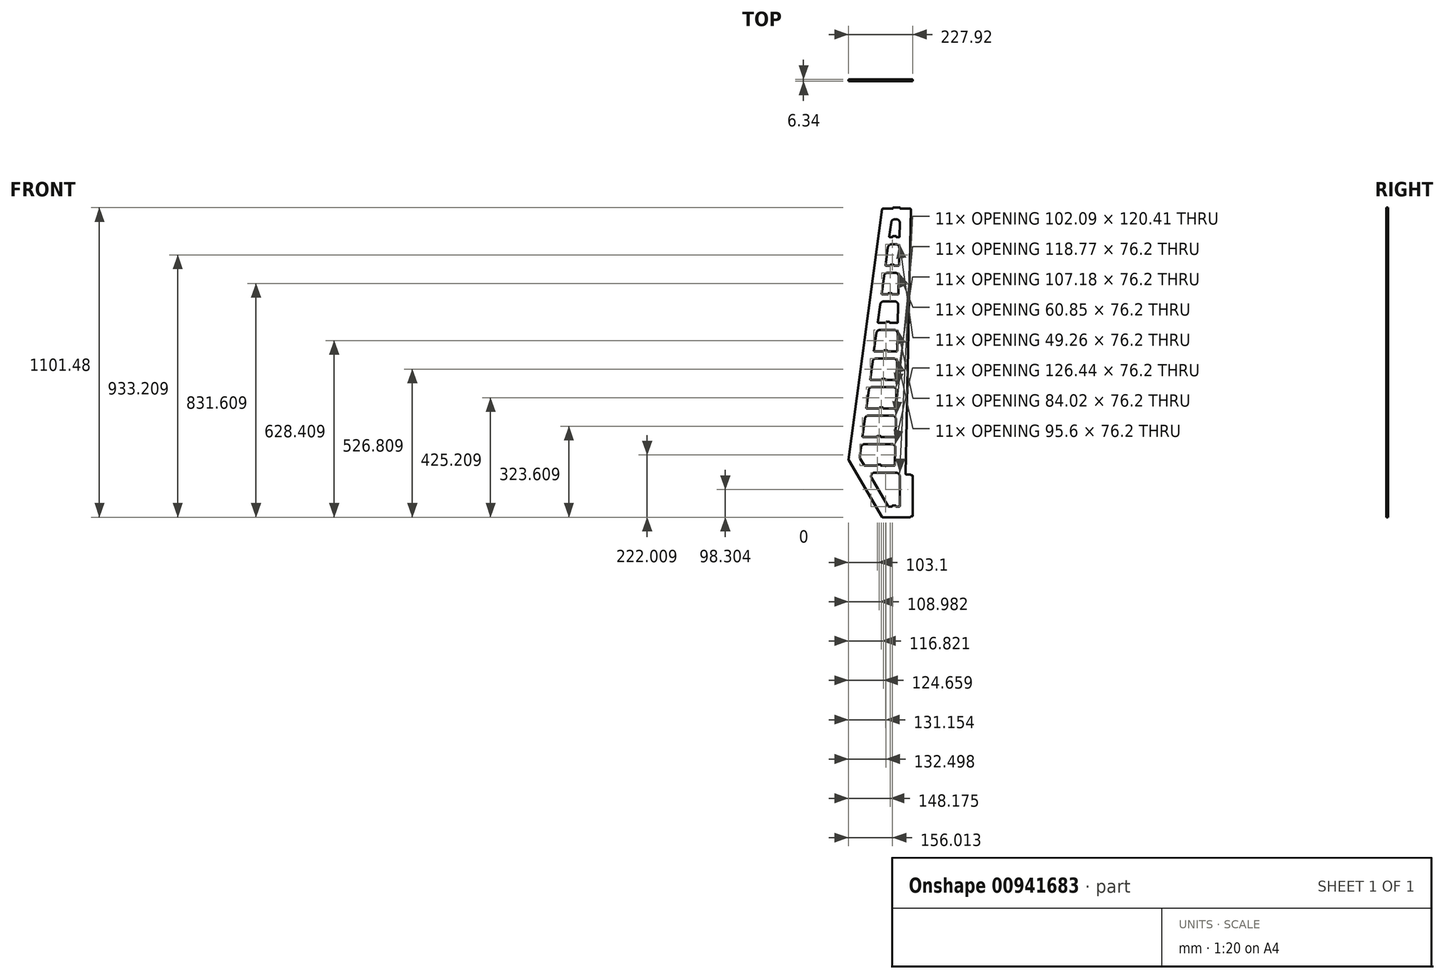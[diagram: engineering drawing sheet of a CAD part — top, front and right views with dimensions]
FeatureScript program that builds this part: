
annotation { "Feature Type Name" : "Feature", "Feature Type Description" : "" }
export const myFeature = defineFeature(function(context is Context, id is Id, definition is map)
    precondition{}
    {
        {
            var Q0;
            Q0=qCreatedBy(makeId("Front.planeOp"),FACE);
            var sketch = newSketch(context, id + "F0", { "sketchPlane" : qUnion([Q0])});
            skLineSegment(sketch, "E0", {"start": v(-3.18, 152.4) * mm, "end": v(-15.81, 152.4) * mm});
            skLineSegment(sketch, "E1", {"start": v(-18.98, 155.64) * mm, "end": v(-0.07, 1095.07) * mm});
            skLineSegment(sketch, "E2", {"start": v(-3.24, 1098.3) * mm, "end": v(-37.78, 1098.3) * mm});
            skLineSegment(sketch, "E3", {"start": v(-101.97, 1095.56) * mm, "end": v(-221.54, 204.3) * mm});
            skLineSegment(sketch, "E4", {"start": v(-221.13, 202.25) * mm, "end": v(-102.52, 1.56) * mm});
            skLineSegment(sketch, "E5", {"start": v(-99.79, 0) * mm, "end": v(-3.17, 0) * mm});
            skLineSegment(sketch, "E6.1", {"start": v(-39.37, 39.69) * mm, "end": v(-39.37, 145.8) * mm});
            skLineSegment(sketch, "E6.2", {"start": v(-51.83, 1060.2) * mm, "end": v(-57.16, 1060.2) * mm});
            skLineSegment(sketch, "E6.3", {"start": v(-69.75, 1049.2) * mm, "end": v(-76.55, 998.5) * mm});
            skLineSegment(sketch, "E6.4", {"start": v(-179.93, 207.43) * mm, "end": v(-166.5, 184.69) * mm});
            skLineSegment(sketch, "E6.5", {"start": v(-56.5, 185.46) * mm, "end": v(-55.25, 247.15) * mm});
            skLineSegment(sketch, "E6.6", {"start": v(-78.95, 38.1) * mm, "end": v(-66.65, 38.1) * mm});
            skLineSegment(sketch, "E7", {"start": v(-41.7, 996.7) * mm, "end": v(-51.8, 996.7) * mm});
            skLineSegment(sketch, "E8", {"start": v(-43.76, 895.1) * mm, "end": v(-59.65, 895.1) * mm});
            skLineSegment(sketch, "E9", {"start": v(-45.8, 793.5) * mm, "end": v(-67.49, 793.5) * mm});
            skLineSegment(sketch, "E10", {"start": v(-47.85, 691.9) * mm, "end": v(-75.33, 691.9) * mm});
            skLineSegment(sketch, "E11", {"start": v(-49.9, 590.3) * mm, "end": v(-83.17, 590.3) * mm});
            skLineSegment(sketch, "E12", {"start": v(-51.94, 488.7) * mm, "end": v(-91.02, 488.7) * mm});
            skLineSegment(sketch, "E13", {"start": v(-53.99, 387.1) * mm, "end": v(-98.86, 387.1) * mm});
            skLineSegment(sketch, "E14", {"start": v(-56.03, 285.5) * mm, "end": v(-106.7, 285.5) * mm});
            skLineSegment(sketch, "E15", {"start": v(-58.08, 183.9) * mm, "end": v(-107, 183.9) * mm});
            skLineSegment(sketch, "E16.0", {"start": v(-52.07, 158.5) * mm, "end": v(-128.76, 158.5) * mm});
            skLineSegment(sketch, "E17.trimOffspring", {"start": v(-139.7, 139.35) * mm, "end": v(-80.32, 38.88) * mm});
            skLineSegment(sketch, "E18.0", {"start": v(-67.95, 260.1) * mm, "end": v(-164.5, 260.1) * mm});
            skLineSegment(sketch, "E19.trimOffspring", {"start": v(-54.45, 287.06) * mm, "end": v(-53.2, 348.75) * mm});
            skLineSegment(sketch, "E20.0", {"start": v(-65.9, 361.7) * mm, "end": v(-150.87, 361.7) * mm});
            skLineSegment(sketch, "E21.trimOffspring", {"start": v(-163.46, 350.7) * mm, "end": v(-172.2, 285.5) * mm});
            skLineSegment(sketch, "E22.trimOffspring", {"start": v(-52.4, 388.66) * mm, "end": v(-51.16, 450.35) * mm});
            skLineSegment(sketch, "E23.0", {"start": v(-63.85, 463.3) * mm, "end": v(-137.24, 463.3) * mm});
            skLineSegment(sketch, "E24.0", {"start": v(-61.8, 564.9) * mm, "end": v(-123.6, 564.9) * mm});
            skLineSegment(sketch, "E25.0", {"start": v(-59.76, 666.5) * mm, "end": v(-109.98, 666.5) * mm});
            skLineSegment(sketch, "E26.0", {"start": v(-57.72, 768.1) * mm, "end": v(-96.35, 768.1) * mm});
            skLineSegment(sketch, "E27.0", {"start": v(-55.67, 869.7) * mm, "end": v(-82.72, 869.7) * mm});
            skLineSegment(sketch, "E28.0", {"start": v(-53.62, 971.3) * mm, "end": v(-69.09, 971.3) * mm});
            skLineSegment(sketch, "E29.trimOffspring", {"start": v(-149.83, 452.3) * mm, "end": v(-158.33, 388.9) * mm});
            skLineSegment(sketch, "E30.trimOffspring", {"start": v(-50.35, 490.26) * mm, "end": v(-49.11, 551.95) * mm});
            skLineSegment(sketch, "E31.trimOffspring", {"start": v(-48.3, 591.86) * mm, "end": v(-47.06, 653.55) * mm});
            skLineSegment(sketch, "E32.trimOffspring", {"start": v(-136.2, 553.9) * mm, "end": v(-144.7, 490.5) * mm});
            skLineSegment(sketch, "E33.trimOffspring", {"start": v(-46.26, 693.46) * mm, "end": v(-45.02, 755.15) * mm});
            skLineSegment(sketch, "E34.trimOffspring", {"start": v(-122.57, 655.5) * mm, "end": v(-131.07, 592.1) * mm});
            skLineSegment(sketch, "E35.trimOffspring", {"start": v(-44.21, 795.06) * mm, "end": v(-42.97, 856.75) * mm});
            skLineSegment(sketch, "E36.trimOffspring", {"start": v(-108.94, 757.1) * mm, "end": v(-117.44, 693.7) * mm});
            skLineSegment(sketch, "E37.trimOffspring", {"start": v(-42.17, 896.66) * mm, "end": v(-40.93, 958.35) * mm});
            skLineSegment(sketch, "E38.trimOffspring", {"start": v(-95.3, 858.7) * mm, "end": v(-103.8, 795.3) * mm});
            skLineSegment(sketch, "E39.trimOffspring", {"start": v(-40.12, 998.26) * mm, "end": v(-39.14, 1047.25) * mm});
            skLineSegment(sketch, "E40.trimOffspring", {"start": v(-81.67, 960.3) * mm, "end": v(-90.18, 896.9) * mm});
            skPoint(sketch, "E41.visualSharp", {"position": v(-161.98, 361.7) * mm});
            skArc(sketch, "E41.filletArc", {"start": v(-150.87, 361.7) * mm, "mid": v(-159.23, 358.57) * mm, "end": v(-163.46, 350.7) * mm});
            skArc(sketch, "E42.filletArc", {"start": v(-53.2, 348.75) * mm, "mid": v(-56.83, 357.9) * mm, "end": v(-65.9, 361.7) * mm});
            skArc(sketch, "E43.filletArc", {"start": v(-51.16, 450.35) * mm, "mid": v(-54.78, 459.5) * mm, "end": v(-63.85, 463.3) * mm});
            skPoint(sketch, "E44.visualSharp", {"position": v(-148.35, 463.3) * mm});
            skArc(sketch, "E44.filletArc", {"start": v(-137.24, 463.3) * mm, "mid": v(-145.6, 460.17) * mm, "end": v(-149.83, 452.3) * mm});
            skPoint(sketch, "E45.visualSharp", {"position": v(-211.06, 260.1) * mm});
            skArc(sketch, "E46.filletArc", {"start": v(-55.25, 247.15) * mm, "mid": v(-58.88, 256.3) * mm, "end": v(-67.95, 260.1) * mm});
            skPoint(sketch, "E47.visualSharp", {"position": v(-39.37, 158.5) * mm});
            skArc(sketch, "E47.filletArc", {"start": v(-39.37, 145.8) * mm, "mid": v(-43.09, 154.79) * mm, "end": v(-52.07, 158.5) * mm});
            skPoint(sketch, "E48.visualSharp", {"position": v(-151.02, 158.5) * mm});
            skArc(sketch, "E48.filletArc", {"start": v(-128.76, 158.5) * mm, "mid": v(-139.8, 152.1) * mm, "end": v(-139.7, 139.35) * mm});
            skArc(sketch, "E49.filletArc", {"start": v(-49.11, 551.95) * mm, "mid": v(-52.74, 561.1) * mm, "end": v(-61.8, 564.9) * mm});
            skPoint(sketch, "E50.visualSharp", {"position": v(-134.72, 564.9) * mm});
            skArc(sketch, "E50.filletArc", {"start": v(-123.6, 564.9) * mm, "mid": v(-131.97, 561.77) * mm, "end": v(-136.2, 553.9) * mm});
            skPoint(sketch, "E51.visualSharp", {"position": v(-121.09, 666.5) * mm});
            skArc(sketch, "E51.filletArc", {"start": v(-109.98, 666.5) * mm, "mid": v(-118.34, 663.37) * mm, "end": v(-122.57, 655.5) * mm});
            skArc(sketch, "E52.filletArc", {"start": v(-47.06, 653.55) * mm, "mid": v(-50.7, 662.7) * mm, "end": v(-59.76, 666.5) * mm});
            skArc(sketch, "E53.filletArc", {"start": v(-45.02, 755.15) * mm, "mid": v(-48.65, 764.3) * mm, "end": v(-57.72, 768.1) * mm});
            skPoint(sketch, "E54.visualSharp", {"position": v(-107.46, 768.1) * mm});
            skArc(sketch, "E54.filletArc", {"start": v(-96.35, 768.1) * mm, "mid": v(-104.71, 764.97) * mm, "end": v(-108.94, 757.1) * mm});
            skArc(sketch, "E55.filletArc", {"start": v(-42.97, 856.75) * mm, "mid": v(-46.6, 865.9) * mm, "end": v(-55.67, 869.7) * mm});
            skPoint(sketch, "E56.visualSharp", {"position": v(-93.83, 869.7) * mm});
            skArc(sketch, "E56.filletArc", {"start": v(-82.72, 869.7) * mm, "mid": v(-91.08, 866.57) * mm, "end": v(-95.3, 858.7) * mm});
            skArc(sketch, "E57.filletArc", {"start": v(-40.93, 958.35) * mm, "mid": v(-44.55, 967.5) * mm, "end": v(-53.62, 971.3) * mm});
            skPoint(sketch, "E58.visualSharp", {"position": v(-80.2, 971.3) * mm});
            skArc(sketch, "E58.filletArc", {"start": v(-69.09, 971.3) * mm, "mid": v(-77.45, 968.17) * mm, "end": v(-81.67, 960.3) * mm});
            skPoint(sketch, "E59.visualSharp", {"position": v(-68.27, 1060.2) * mm});
            skArc(sketch, "E59.filletArc", {"start": v(-57.16, 1060.2) * mm, "mid": v(-65.52, 1057.07) * mm, "end": v(-69.75, 1049.2) * mm});
            skPoint(sketch, "E60.visualSharp", {"position": v(-38.88, 1060.2) * mm});
            skArc(sketch, "E60.filletArc", {"start": v(-39.14, 1047.25) * mm, "mid": v(-42.76, 1056.4) * mm, "end": v(-51.83, 1060.2) * mm});
            skPoint(sketch, "E61.visualSharp", {"position": v(-19.05, 152.4) * mm});
            skArc(sketch, "E61.filletArc", {"start": v(-18.98, 155.64) * mm, "mid": v(-18.08, 153.35) * mm, "end": v(-15.81, 152.4) * mm});
            skPoint(sketch, "E62.visualSharp", {"position": v(0, 152.4) * mm});
            skArc(sketch, "E62.filletArc", {"start": v(0, 149.22) * mm, "mid": v(-0.93, 151.47) * mm, "end": v(-3.17, 152.4) * mm});
            skPoint(sketch, "E63.visualSharp", {"position": v(0, 0) * mm});
            skArc(sketch, "E63.filletArc", {"start": v(-3.17, 0) * mm, "mid": v(-0.93, 0.93) * mm, "end": v(0, 3.17) * mm});
            skPoint(sketch, "E64.visualSharp", {"position": v(-101.6, 0) * mm});
            skArc(sketch, "E64.filletArc", {"start": v(-102.52, 1.56) * mm, "mid": v(-101.36, 0.42) * mm, "end": v(-99.79, 0) * mm});
            skPoint(sketch, "E65.visualSharp", {"position": v(-221.69, 203.2) * mm});
            skArc(sketch, "E65.filletArc", {"start": v(-221.54, 204.3) * mm, "mid": v(-221.5, 203.24) * mm, "end": v(-221.13, 202.25) * mm});
            skPoint(sketch, "E66.visualSharp", {"position": v(-101.6, 1098.3) * mm});
            skArc(sketch, "E66.filletArc", {"start": v(-98.82, 1098.3) * mm, "mid": v(-100.91, 1097.52) * mm, "end": v(-101.97, 1095.56) * mm});
            skPoint(sketch, "E67.visualSharp", {"position": v(0, 1098.3) * mm});
            skArc(sketch, "E67.filletArc", {"start": v(-0.07, 1095.07) * mm, "mid": v(-0.97, 1097.36) * mm, "end": v(-3.24, 1098.3) * mm});
            skPoint(sketch, "E68.visualSharp", {"position": v(-40.15, 996.7) * mm});
            skArc(sketch, "E68.filletArc", {"start": v(-41.7, 996.7) * mm, "mid": v(-40.6, 997.16) * mm, "end": v(-40.12, 998.26) * mm});
            skPoint(sketch, "E69.visualSharp", {"position": v(-76.79, 996.7) * mm});
            skArc(sketch, "E69.filletArc", {"start": v(-76.55, 998.5) * mm, "mid": v(-76.17, 997.25) * mm, "end": v(-74.97, 996.7) * mm});
            skPoint(sketch, "E70.visualSharp", {"position": v(-90.42, 895.1) * mm});
            skArc(sketch, "E70.filletArc", {"start": v(-90.18, 896.9) * mm, "mid": v(-89.8, 895.65) * mm, "end": v(-88.6, 895.1) * mm});
            skPoint(sketch, "E71.visualSharp", {"position": v(-42.2, 895.1) * mm});
            skArc(sketch, "E71.filletArc", {"start": v(-43.76, 895.1) * mm, "mid": v(-42.64, 895.56) * mm, "end": v(-42.17, 896.66) * mm});
            skPoint(sketch, "E72.visualSharp", {"position": v(-44.25, 793.5) * mm});
            skArc(sketch, "E72.filletArc", {"start": v(-45.8, 793.5) * mm, "mid": v(-44.7, 793.96) * mm, "end": v(-44.21, 795.06) * mm});
            skPoint(sketch, "E73.visualSharp", {"position": v(-104.05, 793.5) * mm});
            skArc(sketch, "E73.filletArc", {"start": v(-103.8, 795.3) * mm, "mid": v(-103.43, 794.05) * mm, "end": v(-102.24, 793.5) * mm});
            skPoint(sketch, "E74.visualSharp", {"position": v(-117.68, 691.9) * mm});
            skArc(sketch, "E74.filletArc", {"start": v(-117.44, 693.7) * mm, "mid": v(-117.06, 692.45) * mm, "end": v(-115.87, 691.9) * mm});
            skPoint(sketch, "E75.visualSharp", {"position": v(-46.3, 691.9) * mm});
            skArc(sketch, "E75.filletArc", {"start": v(-47.85, 691.9) * mm, "mid": v(-46.74, 692.36) * mm, "end": v(-46.26, 693.46) * mm});
            skPoint(sketch, "E76.visualSharp", {"position": v(-48.34, 590.3) * mm});
            skArc(sketch, "E76.filletArc", {"start": v(-49.9, 590.3) * mm, "mid": v(-48.78, 590.76) * mm, "end": v(-48.3, 591.86) * mm});
            skPoint(sketch, "E77.visualSharp", {"position": v(-131.31, 590.3) * mm});
            skArc(sketch, "E77.filletArc", {"start": v(-131.07, 592.1) * mm, "mid": v(-130.7, 590.85) * mm, "end": v(-129.5, 590.3) * mm});
            skPoint(sketch, "E78.visualSharp", {"position": v(-50.38, 488.7) * mm});
            skArc(sketch, "E78.filletArc", {"start": v(-51.94, 488.7) * mm, "mid": v(-50.83, 489.16) * mm, "end": v(-50.35, 490.26) * mm});
            skPoint(sketch, "E79.visualSharp", {"position": v(-144.94, 488.7) * mm});
            skArc(sketch, "E79.filletArc", {"start": v(-144.7, 490.5) * mm, "mid": v(-144.32, 489.25) * mm, "end": v(-143.13, 488.7) * mm});
            skPoint(sketch, "E80.visualSharp", {"position": v(-52.43, 387.1) * mm});
            skArc(sketch, "E80.filletArc", {"start": v(-53.99, 387.1) * mm, "mid": v(-52.88, 387.56) * mm, "end": v(-52.4, 388.66) * mm});
            skPoint(sketch, "E81.visualSharp", {"position": v(-158.57, 387.1) * mm});
            skArc(sketch, "E81.filletArc", {"start": v(-158.33, 388.9) * mm, "mid": v(-157.95, 387.65) * mm, "end": v(-156.76, 387.1) * mm});
            skPoint(sketch, "E82.visualSharp", {"position": v(-54.48, 285.5) * mm});
            skArc(sketch, "E82.filletArc", {"start": v(-56.03, 285.5) * mm, "mid": v(-54.92, 285.96) * mm, "end": v(-54.45, 287.06) * mm});
            skPoint(sketch, "E83.visualSharp", {"position": v(-172.2, 285.5) * mm});
            skArc(sketch, "E83.filletArc", {"start": v(-171.96, 287.3) * mm, "mid": v(-171.58, 286.05) * mm, "end": v(-170.39, 285.5) * mm});
            skPoint(sketch, "E84.visualSharp", {"position": v(-56.52, 183.9) * mm});
            skArc(sketch, "E84.filletArc", {"start": v(-58.08, 183.9) * mm, "mid": v(-56.97, 184.36) * mm, "end": v(-56.5, 185.46) * mm});
            skPoint(sketch, "E85.visualSharp", {"position": v(-79.86, 38.1) * mm});
            skArc(sketch, "E85.filletArc", {"start": v(-80.32, 38.88) * mm, "mid": v(-79.74, 38.3) * mm, "end": v(-78.95, 38.1) * mm});
            skPoint(sketch, "E86.visualSharp", {"position": v(-39.37, 38.1) * mm});
            skArc(sketch, "E86.filletArc", {"start": v(-40.96, 38.1) * mm, "mid": v(-39.83, 38.56) * mm, "end": v(-39.37, 39.69) * mm});
            skLineSegment(sketch, "E87.top", {"start": v(-63.18, 1101.48) * mm, "end": v(-38.42, 1101.48) * mm});
            skLineSegment(sketch, "E87.left", {"start": v(-63.5, 1098.63) * mm, "end": v(-63.5, 1101.17) * mm});
            skLineSegment(sketch, "E87.right", {"start": v(-38.1, 1098.63) * mm, "end": v(-38.1, 1101.17) * mm});
            skLineSegment(sketch, "E88.trimOffspring", {"start": v(-63.82, 1098.3) * mm, "end": v(-98.82, 1098.3) * mm});
            skLineSegment(sketch, "E89.top", {"start": v(-64.5, 999.88) * mm, "end": v(-52.44, 999.88) * mm});
            skLineSegment(sketch, "E89.left", {"start": v(-64.82, 997.03) * mm, "end": v(-64.82, 999.57) * mm});
            skLineSegment(sketch, "E89.right", {"start": v(-52.12, 997.03) * mm, "end": v(-52.12, 999.57) * mm});
            skLineSegment(sketch, "E90.trimOffspring", {"start": v(-65.14, 996.7) * mm, "end": v(-74.97, 996.7) * mm});
            skLineSegment(sketch, "E91.top", {"start": v(-72.35, 898.28) * mm, "end": v(-60.28, 898.28) * mm});
            skLineSegment(sketch, "E91.left", {"start": v(-72.66, 895.43) * mm, "end": v(-72.66, 897.97) * mm});
            skLineSegment(sketch, "E91.right", {"start": v(-59.96, 895.43) * mm, "end": v(-59.96, 897.97) * mm});
            skLineSegment(sketch, "E92.top", {"start": v(-80.19, 796.68) * mm, "end": v(-68.12, 796.68) * mm});
            skLineSegment(sketch, "E92.left", {"start": v(-80.5, 793.83) * mm, "end": v(-80.5, 796.37) * mm});
            skLineSegment(sketch, "E92.right", {"start": v(-67.8, 793.83) * mm, "end": v(-67.8, 796.37) * mm});
            skLineSegment(sketch, "E93.trimOffspring", {"start": v(-80.82, 793.5) * mm, "end": v(-102.24, 793.5) * mm});
            skLineSegment(sketch, "E94.trimOffspring", {"start": v(-72.98, 895.1) * mm, "end": v(-88.6, 895.1) * mm});
            skLineSegment(sketch, "E95.top", {"start": v(-88.03, 695.08) * mm, "end": v(-75.97, 695.08) * mm});
            skLineSegment(sketch, "E95.left", {"start": v(-88.35, 692.23) * mm, "end": v(-88.35, 694.77) * mm});
            skLineSegment(sketch, "E95.right", {"start": v(-75.65, 692.23) * mm, "end": v(-75.65, 694.77) * mm});
            skLineSegment(sketch, "E96.top", {"start": v(-95.87, 593.48) * mm, "end": v(-83.8, 593.48) * mm});
            skLineSegment(sketch, "E96.left", {"start": v(-96.2, 590.63) * mm, "end": v(-96.2, 593.17) * mm});
            skLineSegment(sketch, "E96.right", {"start": v(-83.5, 590.63) * mm, "end": v(-83.5, 593.17) * mm});
            skLineSegment(sketch, "E97.trimOffspring", {"start": v(-96.5, 590.3) * mm, "end": v(-129.5, 590.3) * mm});
            skLineSegment(sketch, "E98.trimOffspring", {"start": v(-88.67, 691.9) * mm, "end": v(-115.87, 691.9) * mm});
            skLineSegment(sketch, "E99.top", {"start": v(-103.72, 491.88) * mm, "end": v(-91.65, 491.88) * mm});
            skLineSegment(sketch, "E99.left", {"start": v(-104.03, 489.03) * mm, "end": v(-104.03, 491.57) * mm});
            skLineSegment(sketch, "E99.right", {"start": v(-91.33, 489.03) * mm, "end": v(-91.33, 491.57) * mm});
            skLineSegment(sketch, "E100.trimOffspring", {"start": v(-104.35, 488.7) * mm, "end": v(-143.13, 488.7) * mm});
            skLineSegment(sketch, "E101.top", {"start": v(-111.56, 390.28) * mm, "end": v(-99.5, 390.28) * mm});
            skLineSegment(sketch, "E101.left", {"start": v(-111.87, 387.43) * mm, "end": v(-111.87, 389.97) * mm});
            skLineSegment(sketch, "E101.right", {"start": v(-99.17, 387.43) * mm, "end": v(-99.17, 389.97) * mm});
            skLineSegment(sketch, "E102.trimOffspring", {"start": v(-112.2, 387.1) * mm, "end": v(-156.76, 387.1) * mm});
            skLineSegment(sketch, "E103.top", {"start": v(-119.4, 288.68) * mm, "end": v(-107.33, 288.68) * mm});
            skLineSegment(sketch, "E103.left", {"start": v(-119.72, 285.83) * mm, "end": v(-119.72, 288.37) * mm});
            skLineSegment(sketch, "E103.right", {"start": v(-107.02, 285.83) * mm, "end": v(-107.02, 288.37) * mm});
            skLineSegment(sketch, "E104.trimOffspring", {"start": v(-120.03, 285.5) * mm, "end": v(-170.39, 285.5) * mm});
            skLineSegment(sketch, "E105.top", {"start": v(-119.7, 187.08) * mm, "end": v(-107.64, 187.08) * mm});
            skLineSegment(sketch, "E105.left", {"start": v(-120.02, 184.23) * mm, "end": v(-120.02, 186.77) * mm});
            skLineSegment(sketch, "E105.right", {"start": v(-107.32, 184.23) * mm, "end": v(-107.32, 186.77) * mm});
            skPoint(sketch, "E106.visualSharp", {"position": v(-166.03, 183.9) * mm});
            skArc(sketch, "E106.filletArc", {"start": v(-166.5, 184.69) * mm, "mid": v(-165.91, 184.12) * mm, "end": v(-165.13, 183.9) * mm});
            skLineSegment(sketch, "E107.trimOffspring", {"start": v(-120.34, 183.9) * mm, "end": v(-165.13, 183.9) * mm});
            skLineSegment(sketch, "E108.top", {"start": v(-53.95, 41.27) * mm, "end": v(-66.01, 41.27) * mm});
            skLineSegment(sketch, "E108.left", {"start": v(-53.63, 38.42) * mm, "end": v(-53.63, 40.96) * mm});
            skLineSegment(sketch, "E108.right", {"start": v(-66.33, 38.42) * mm, "end": v(-66.33, 40.96) * mm});
            skLineSegment(sketch, "E109.trimOffspring", {"start": v(-53.31, 38.1) * mm, "end": v(-40.96, 38.1) * mm});
            skLineSegment(sketch, "E110.bottom", {"start": v(0, 149.22) * mm, "end": v(4.76, 149.22) * mm});
            skLineSegment(sketch, "E110.top", {"start": v(0, 3.17) * mm, "end": v(4.76, 3.17) * mm});
            skLineSegment(sketch, "E110.right", {"start": v(6.35, 147.64) * mm, "end": v(6.35, 4.76) * mm});
            skPoint(sketch, "E111.visualSharp", {"position": v(6.35, 149.22) * mm});
            skArc(sketch, "E111.filletArc", {"start": v(6.35, 147.64) * mm, "mid": v(5.89, 148.76) * mm, "end": v(4.76, 149.22) * mm});
            skPoint(sketch, "E112.visualSharp", {"position": v(6.35, 3.17) * mm});
            skArc(sketch, "E112.filletArc", {"start": v(4.76, 3.18) * mm, "mid": v(5.89, 3.64) * mm, "end": v(6.35, 4.76) * mm});
            skPoint(sketch, "E113.visualSharp", {"position": v(-66.33, 38.1) * mm});
            skArc(sketch, "E113.filletArc", {"start": v(-66.65, 38.1) * mm, "mid": v(-66.42, 38.2) * mm, "end": v(-66.33, 38.42) * mm});
            skPoint(sketch, "E114.visualSharp", {"position": v(-66.33, 41.27) * mm});
            skArc(sketch, "E114.filletArc", {"start": v(-66.01, 41.27) * mm, "mid": v(-66.24, 41.18) * mm, "end": v(-66.33, 40.96) * mm});
            skPoint(sketch, "E115.visualSharp", {"position": v(-53.63, 41.27) * mm});
            skArc(sketch, "E115.filletArc", {"start": v(-53.63, 40.96) * mm, "mid": v(-53.72, 41.18) * mm, "end": v(-53.95, 41.27) * mm});
            skPoint(sketch, "E116.visualSharp", {"position": v(-53.63, 38.1) * mm});
            skArc(sketch, "E116.filletArc", {"start": v(-53.63, 38.42) * mm, "mid": v(-53.54, 38.2) * mm, "end": v(-53.31, 38.1) * mm});
            skPoint(sketch, "E117.visualSharp", {"position": v(-107.32, 183.9) * mm});
            skArc(sketch, "E117.filletArc", {"start": v(-107.32, 184.23) * mm, "mid": v(-107.23, 184) * mm, "end": v(-107, 183.9) * mm});
            skPoint(sketch, "E118.visualSharp", {"position": v(-107.32, 187.08) * mm});
            skArc(sketch, "E118.filletArc", {"start": v(-107.32, 186.77) * mm, "mid": v(-107.42, 187) * mm, "end": v(-107.64, 187.08) * mm});
            skPoint(sketch, "E119.visualSharp", {"position": v(-120.02, 187.08) * mm});
            skArc(sketch, "E119.filletArc", {"start": v(-119.7, 187.08) * mm, "mid": v(-119.93, 187) * mm, "end": v(-120.02, 186.77) * mm});
            skPoint(sketch, "E120.visualSharp", {"position": v(-120.02, 183.9) * mm});
            skArc(sketch, "E120.filletArc", {"start": v(-120.34, 183.9) * mm, "mid": v(-120.12, 184) * mm, "end": v(-120.02, 184.23) * mm});
            skPoint(sketch, "E121.visualSharp", {"position": v(-119.72, 288.68) * mm});
            skArc(sketch, "E121.filletArc", {"start": v(-119.4, 288.68) * mm, "mid": v(-119.62, 288.6) * mm, "end": v(-119.72, 288.37) * mm});
            skPoint(sketch, "E122.visualSharp", {"position": v(-119.72, 285.5) * mm});
            skArc(sketch, "E122.filletArc", {"start": v(-120.03, 285.5) * mm, "mid": v(-119.8, 285.6) * mm, "end": v(-119.72, 285.83) * mm});
            skPoint(sketch, "E123.visualSharp", {"position": v(-107.02, 288.68) * mm});
            skArc(sketch, "E123.filletArc", {"start": v(-107.02, 288.37) * mm, "mid": v(-107.1, 288.6) * mm, "end": v(-107.33, 288.68) * mm});
            skPoint(sketch, "E124.visualSharp", {"position": v(-107.02, 285.5) * mm});
            skArc(sketch, "E124.filletArc", {"start": v(-107.02, 285.83) * mm, "mid": v(-106.92, 285.6) * mm, "end": v(-106.7, 285.5) * mm});
            skPoint(sketch, "E125.visualSharp", {"position": v(-99.17, 390.28) * mm});
            skArc(sketch, "E125.filletArc", {"start": v(-99.17, 389.97) * mm, "mid": v(-99.27, 390.2) * mm, "end": v(-99.5, 390.28) * mm});
            skPoint(sketch, "E126.visualSharp", {"position": v(-99.17, 387.1) * mm});
            skArc(sketch, "E126.filletArc", {"start": v(-99.17, 387.43) * mm, "mid": v(-99.08, 387.2) * mm, "end": v(-98.86, 387.1) * mm});
            skPoint(sketch, "E127.visualSharp", {"position": v(-111.87, 387.1) * mm});
            skArc(sketch, "E127.filletArc", {"start": v(-112.2, 387.1) * mm, "mid": v(-111.97, 387.2) * mm, "end": v(-111.87, 387.43) * mm});
            skPoint(sketch, "E128.visualSharp", {"position": v(-111.87, 390.28) * mm});
            skArc(sketch, "E128.filletArc", {"start": v(-111.56, 390.28) * mm, "mid": v(-111.78, 390.2) * mm, "end": v(-111.87, 389.97) * mm});
            skPoint(sketch, "E129.visualSharp", {"position": v(-91.33, 488.7) * mm});
            skArc(sketch, "E129.filletArc", {"start": v(-91.33, 489.03) * mm, "mid": v(-91.24, 488.8) * mm, "end": v(-91.02, 488.7) * mm});
            skPoint(sketch, "E130.visualSharp", {"position": v(-91.33, 491.88) * mm});
            skArc(sketch, "E130.filletArc", {"start": v(-91.33, 491.57) * mm, "mid": v(-91.43, 491.8) * mm, "end": v(-91.65, 491.88) * mm});
            skPoint(sketch, "E131.visualSharp", {"position": v(-104.03, 491.88) * mm});
            skArc(sketch, "E131.filletArc", {"start": v(-103.72, 491.88) * mm, "mid": v(-103.94, 491.8) * mm, "end": v(-104.03, 491.57) * mm});
            skPoint(sketch, "E132.visualSharp", {"position": v(-104.03, 488.7) * mm});
            skArc(sketch, "E132.filletArc", {"start": v(-104.35, 488.7) * mm, "mid": v(-104.13, 488.8) * mm, "end": v(-104.03, 489.03) * mm});
            skPoint(sketch, "E133.visualSharp", {"position": v(-83.5, 590.3) * mm});
            skArc(sketch, "E133.filletArc", {"start": v(-83.5, 590.63) * mm, "mid": v(-83.4, 590.4) * mm, "end": v(-83.17, 590.3) * mm});
            skPoint(sketch, "E134.visualSharp", {"position": v(-83.5, 593.48) * mm});
            skArc(sketch, "E134.filletArc", {"start": v(-83.5, 593.17) * mm, "mid": v(-83.58, 593.4) * mm, "end": v(-83.8, 593.48) * mm});
            skPoint(sketch, "E135.visualSharp", {"position": v(-96.2, 593.48) * mm});
            skArc(sketch, "E135.filletArc", {"start": v(-95.87, 593.48) * mm, "mid": v(-96.1, 593.4) * mm, "end": v(-96.2, 593.17) * mm});
            skPoint(sketch, "E136.visualSharp", {"position": v(-96.2, 590.3) * mm});
            skArc(sketch, "E136.filletArc", {"start": v(-96.5, 590.3) * mm, "mid": v(-96.28, 590.4) * mm, "end": v(-96.2, 590.63) * mm});
            skPoint(sketch, "E137.visualSharp", {"position": v(-75.65, 695.08) * mm});
            skArc(sketch, "E137.filletArc", {"start": v(-75.65, 694.77) * mm, "mid": v(-75.74, 695) * mm, "end": v(-75.97, 695.08) * mm});
            skPoint(sketch, "E138.visualSharp", {"position": v(-75.65, 691.9) * mm});
            skArc(sketch, "E138.filletArc", {"start": v(-75.65, 692.23) * mm, "mid": v(-75.56, 692) * mm, "end": v(-75.33, 691.9) * mm});
            skPoint(sketch, "E139.visualSharp", {"position": v(-88.35, 691.9) * mm});
            skArc(sketch, "E139.filletArc", {"start": v(-88.67, 691.9) * mm, "mid": v(-88.44, 692) * mm, "end": v(-88.35, 692.23) * mm});
            skPoint(sketch, "E140.visualSharp", {"position": v(-88.35, 695.08) * mm});
            skArc(sketch, "E140.filletArc", {"start": v(-88.03, 695.08) * mm, "mid": v(-88.26, 695) * mm, "end": v(-88.35, 694.77) * mm});
            skPoint(sketch, "E141.visualSharp", {"position": v(-67.8, 796.68) * mm});
            skArc(sketch, "E141.filletArc", {"start": v(-67.8, 796.37) * mm, "mid": v(-67.9, 796.6) * mm, "end": v(-68.12, 796.68) * mm});
            skPoint(sketch, "E142.visualSharp", {"position": v(-67.8, 793.5) * mm});
            skArc(sketch, "E142.filletArc", {"start": v(-67.8, 793.83) * mm, "mid": v(-67.71, 793.6) * mm, "end": v(-67.49, 793.5) * mm});
            skPoint(sketch, "E143.visualSharp", {"position": v(-80.5, 793.5) * mm});
            skArc(sketch, "E143.filletArc", {"start": v(-80.82, 793.5) * mm, "mid": v(-80.6, 793.6) * mm, "end": v(-80.5, 793.83) * mm});
            skPoint(sketch, "E144.visualSharp", {"position": v(-80.5, 796.68) * mm});
            skArc(sketch, "E144.filletArc", {"start": v(-80.19, 796.68) * mm, "mid": v(-80.41, 796.6) * mm, "end": v(-80.5, 796.37) * mm});
            skPoint(sketch, "E145.visualSharp", {"position": v(-59.96, 895.1) * mm});
            skArc(sketch, "E145.filletArc", {"start": v(-59.96, 895.43) * mm, "mid": v(-59.87, 895.2) * mm, "end": v(-59.65, 895.1) * mm});
            skPoint(sketch, "E146.visualSharp", {"position": v(-72.66, 898.28) * mm});
            skArc(sketch, "E146.filletArc", {"start": v(-72.35, 898.28) * mm, "mid": v(-72.57, 898.2) * mm, "end": v(-72.66, 897.97) * mm});
            skPoint(sketch, "E147.visualSharp", {"position": v(-72.66, 895.1) * mm});
            skArc(sketch, "E147.filletArc", {"start": v(-72.98, 895.1) * mm, "mid": v(-72.76, 895.2) * mm, "end": v(-72.66, 895.43) * mm});
            skPoint(sketch, "E148.visualSharp", {"position": v(-59.96, 898.28) * mm});
            skArc(sketch, "E148.filletArc", {"start": v(-59.96, 897.97) * mm, "mid": v(-60.06, 898.2) * mm, "end": v(-60.28, 898.28) * mm});
            skPoint(sketch, "E149.visualSharp", {"position": v(-52.12, 999.88) * mm});
            skArc(sketch, "E149.filletArc", {"start": v(-52.12, 999.57) * mm, "mid": v(-52.21, 999.8) * mm, "end": v(-52.44, 999.88) * mm});
            skPoint(sketch, "E150.visualSharp", {"position": v(-52.12, 996.7) * mm});
            skArc(sketch, "E150.filletArc", {"start": v(-52.12, 997.03) * mm, "mid": v(-52.03, 996.8) * mm, "end": v(-51.8, 996.7) * mm});
            skPoint(sketch, "E151.visualSharp", {"position": v(-64.82, 996.7) * mm});
            skArc(sketch, "E151.filletArc", {"start": v(-65.14, 996.7) * mm, "mid": v(-64.91, 996.8) * mm, "end": v(-64.82, 997.03) * mm});
            skPoint(sketch, "E152.visualSharp", {"position": v(-64.82, 999.88) * mm});
            skArc(sketch, "E152.filletArc", {"start": v(-64.5, 999.88) * mm, "mid": v(-64.73, 999.8) * mm, "end": v(-64.82, 999.57) * mm});
            skPoint(sketch, "E153.visualSharp", {"position": v(-63.5, 1101.48) * mm});
            skArc(sketch, "E153.filletArc", {"start": v(-63.18, 1101.48) * mm, "mid": v(-63.4, 1101.4) * mm, "end": v(-63.5, 1101.17) * mm});
            skPoint(sketch, "E154.visualSharp", {"position": v(-63.5, 1098.3) * mm});
            skArc(sketch, "E154.filletArc", {"start": v(-63.82, 1098.3) * mm, "mid": v(-63.6, 1098.4) * mm, "end": v(-63.5, 1098.63) * mm});
            skPoint(sketch, "E155.visualSharp", {"position": v(-38.1, 1101.48) * mm});
            skArc(sketch, "E155.filletArc", {"start": v(-38.1, 1101.17) * mm, "mid": v(-38.2, 1101.4) * mm, "end": v(-38.42, 1101.48) * mm});
            skPoint(sketch, "E156.visualSharp", {"position": v(-38.1, 1098.3) * mm});
            skArc(sketch, "E156.filletArc", {"start": v(-38.1, 1098.63) * mm, "mid": v(-38, 1098.4) * mm, "end": v(-37.78, 1098.3) * mm});
            skLineSegment(sketch, "E157.trimOffspring", {"start": v(-177.09, 249.1) * mm, "end": v(-181.59, 215.58) * mm});
            skPoint(sketch, "E158.visualSharp", {"position": v(-175.61, 260.1) * mm});
            skArc(sketch, "E158.filletArc", {"start": v(-164.5, 260.1) * mm, "mid": v(-172.86, 256.97) * mm, "end": v(-177.09, 249.1) * mm});
            skPoint(sketch, "E159.visualSharp", {"position": v(-182.17, 211.22) * mm});
            skArc(sketch, "E159.filletArc", {"start": v(-181.59, 215.58) * mm, "mid": v(-181.44, 211.37) * mm, "end": v(-179.93, 207.43) * mm});
            skSolve(sketch);
        }
        {
            var Q0;
            Q0=makeQuery(id+"F0.imprint","IMPRINT",FACE,{"disambiguationData":[TD([[makeQuery(id+"F0.imprint","IMPRINT",EDGE,{"derivedFrom":sQuery(id+"F0.wireOp",EDGE,"E0")}),1.0]])]});
            extrude(context, id + "F1", {"entities" : qUnion([Q0]), "endBound" : BoundingType.SYMMETRIC, "depth" : 6.35 * mm, "offsetDistance" : 25.4 * mm});
        }
    });
